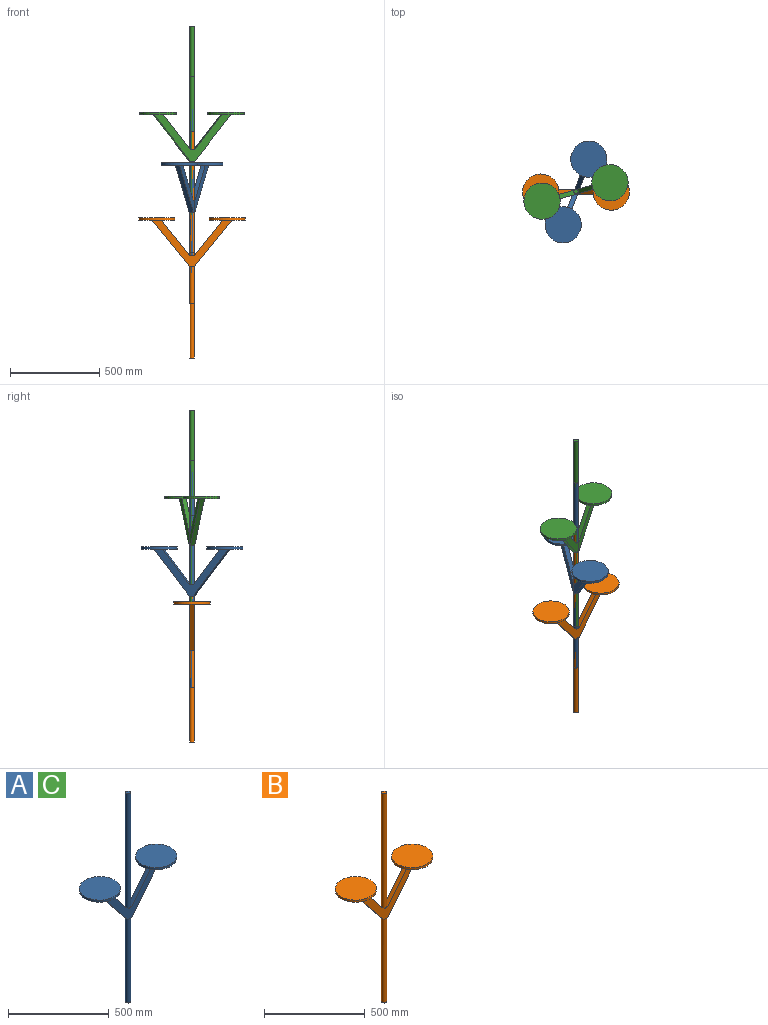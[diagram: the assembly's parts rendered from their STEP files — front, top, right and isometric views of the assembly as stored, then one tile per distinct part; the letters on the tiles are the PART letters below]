
ASSEMBLY  parts=3 mates=2
PART A: 24 faces, bbox 598x203.2x1270 mm
  f0: cylinder r=12.7mm len=694.01mm, axis (0,0,-1), area 55379.3mm2, adj f1,f2,f3,f4,f11
  f1: plane 25.4x25.4mm, normal (0,0,1), area 506.7mm2, adj f0
  f2: plane 12.7x12.7mm, normal (0,0,1), area 34.6mm2, adj f0,f9,f10
  f3: plane 12.7x12.7mm, normal (0,0,1), area 34.6mm2, adj f0,f9,f12
  f4: plane 12.7x12.7mm, normal (0,0,1), area 34.6mm2, adj f0,f8,f12
  f5: plane 12.7x12.7mm, normal (0,0,-1), area 34.6mm2, adj f9,f13,f17
  f6: plane 12.7x12.7mm, normal (0,0,-1), area 34.6mm2, adj f9,f15,f17
  f7: plane 12.7x12.7mm, normal (0,0,-1), area 34.6mm2, adj f8,f15,f17
  f8: plane 447.02x262.76mm, normal (0,-1,0), area 25703.6mm2, adj f4,f7,f10,f11,f12,f13,f14,f15
  f9: plane 447.02x262.76mm, normal (0,1,0), area 25703.6mm2, adj f2,f3,f5,f6,f10,f12,f13,f15
  f10: plane 197.65x158.57mm, normal (-0.78,0,0.63), area 6436.3mm2, adj f2,f8,f9,f11,f23
  f11: plane 12.7x12.7mm, normal (0,0,1), area 34.6mm2, adj f0,f8,f10
  f12: plane 197.65x158.57mm, normal (0.78,0,0.63), area 6436.3mm2, adj f3,f4,f8,f9,f18
  f13: plane 262.76x210.81mm, normal (-0.78,0,-0.63), area 8556.5mm2, adj f5,f8,f9,f14,f18
  f14: plane 12.7x12.7mm, normal (0,0,-1), area 34.6mm2, adj f8,f13,f17
  f15: plane 262.76x210.81mm, normal (0.78,0,-0.63), area 8556.5mm2, adj f6,f7,f8,f9,f23
  f16: plane 25.4x25.4mm, normal (0,0,-1), area 506.7mm2, adj f17
  f17: cylinder r=12.7mm len=510.88mm, axis (0,0,-1), area 40766.8mm2, adj f5,f6,f7,f14,f16
  f18: plane 203.2x203.2mm, normal (0,0,-1), area 31102.5mm2, adj f8,f9,f12,f13,f19
  f19: cylinder r=101.6mm len=203.2mm, axis (0,0,-1), area 8107.3mm2, adj f18,f20
  f20: plane 203.2x203.2mm, normal (0,0,1), area 32429.3mm2, adj f19
  f21: cylinder r=101.6mm len=203.2mm, axis (0,0,-1), area 8107.3mm2, adj f22,f23
  f22: plane 203.2x203.2mm, normal (0,0,1), area 32429.3mm2, adj f21
  f23: plane 203.2x203.2mm, normal (0,0,-1), area 31102.5mm2, adj f8,f9,f10,f15,f21
PART B: 24 faces, bbox 598x203.2x1270 mm
  f0: cylinder r=12.7mm len=694.01mm, axis (0,0,-1), area 55379.3mm2, adj f1,f2,f3,f4,f11
  f1: plane 25.4x25.4mm, normal (0,0,1), area 506.7mm2, adj f0
  f2: plane 12.7x12.7mm, normal (0,0,1), area 34.6mm2, adj f0,f9,f10
  f3: plane 12.7x12.7mm, normal (0,0,1), area 34.6mm2, adj f0,f9,f12
  f4: plane 12.7x12.7mm, normal (0,0,1), area 34.6mm2, adj f0,f8,f12
  f5: plane 12.7x12.7mm, normal (0,0,-1), area 34.6mm2, adj f9,f13,f17
  f6: plane 12.7x12.7mm, normal (0,0,-1), area 34.6mm2, adj f9,f15,f17
  f7: plane 12.7x12.7mm, normal (0,0,-1), area 34.6mm2, adj f8,f15,f17
  f8: plane 447.02x262.76mm, normal (0,-1,0), area 25703.6mm2, adj f4,f7,f10,f11,f12,f13,f14,f15
  f9: plane 447.02x262.76mm, normal (0,1,0), area 25703.6mm2, adj f2,f3,f5,f6,f10,f12,f13,f15
  f10: plane 197.65x158.57mm, normal (-0.78,0,0.63), area 6436.3mm2, adj f2,f8,f9,f11,f23
  f11: plane 12.7x12.7mm, normal (0,0,1), area 34.6mm2, adj f0,f8,f10
  f12: plane 197.65x158.57mm, normal (0.78,0,0.63), area 6436.3mm2, adj f3,f4,f8,f9,f18
  f13: plane 262.76x210.81mm, normal (-0.78,0,-0.63), area 8556.5mm2, adj f5,f8,f9,f14,f18
  f14: plane 12.7x12.7mm, normal (0,0,-1), area 34.6mm2, adj f8,f13,f17
  f15: plane 262.76x210.81mm, normal (0.78,0,-0.63), area 8556.5mm2, adj f6,f7,f8,f9,f23
  f16: plane 25.4x25.4mm, normal (0,0,-1), area 506.7mm2, adj f17
  f17: cylinder r=12.7mm len=510.88mm, axis (0,0,-1), area 40766.8mm2, adj f5,f6,f7,f14,f16
  f18: plane 203.2x203.2mm, normal (0,0,-1), area 31102.5mm2, adj f8,f9,f12,f13,f19
  f19: cylinder r=101.6mm len=203.2mm, axis (0,0,-1), area 8107.3mm2, adj f18,f20
  f20: plane 203.2x203.2mm, normal (0,0,1), area 32429.3mm2, adj f19
  f21: cylinder r=101.6mm len=203.2mm, axis (0,0,-1), area 8107.3mm2, adj f22,f23
  f22: plane 203.2x203.2mm, normal (0,0,1), area 32429.3mm2, adj f21
  f23: plane 203.2x203.2mm, normal (0,0,-1), area 31102.5mm2, adj f8,f9,f10,f15,f21
PART C: same geometry as A
PLACE A rot(axis=(0,0,1),68.6deg) t=(-582.73,-168.72,368.69)mm
PLACE B t=(-582.73,-168.72,442.08)mm fixed
PLACE C rot(axis=(0,0,-1),164.8deg) t=(-582.73,-168.72,652.86)mm
MATE cylindrical B.f0 <-> A.f0  axis (0,0,-1) through (-582.73,-168.72,-318.48)mm
MATE cylindrical C.f0 <-> A.f0  axis (0,0,-1) through (-582.73,-168.72,528.75)mm
